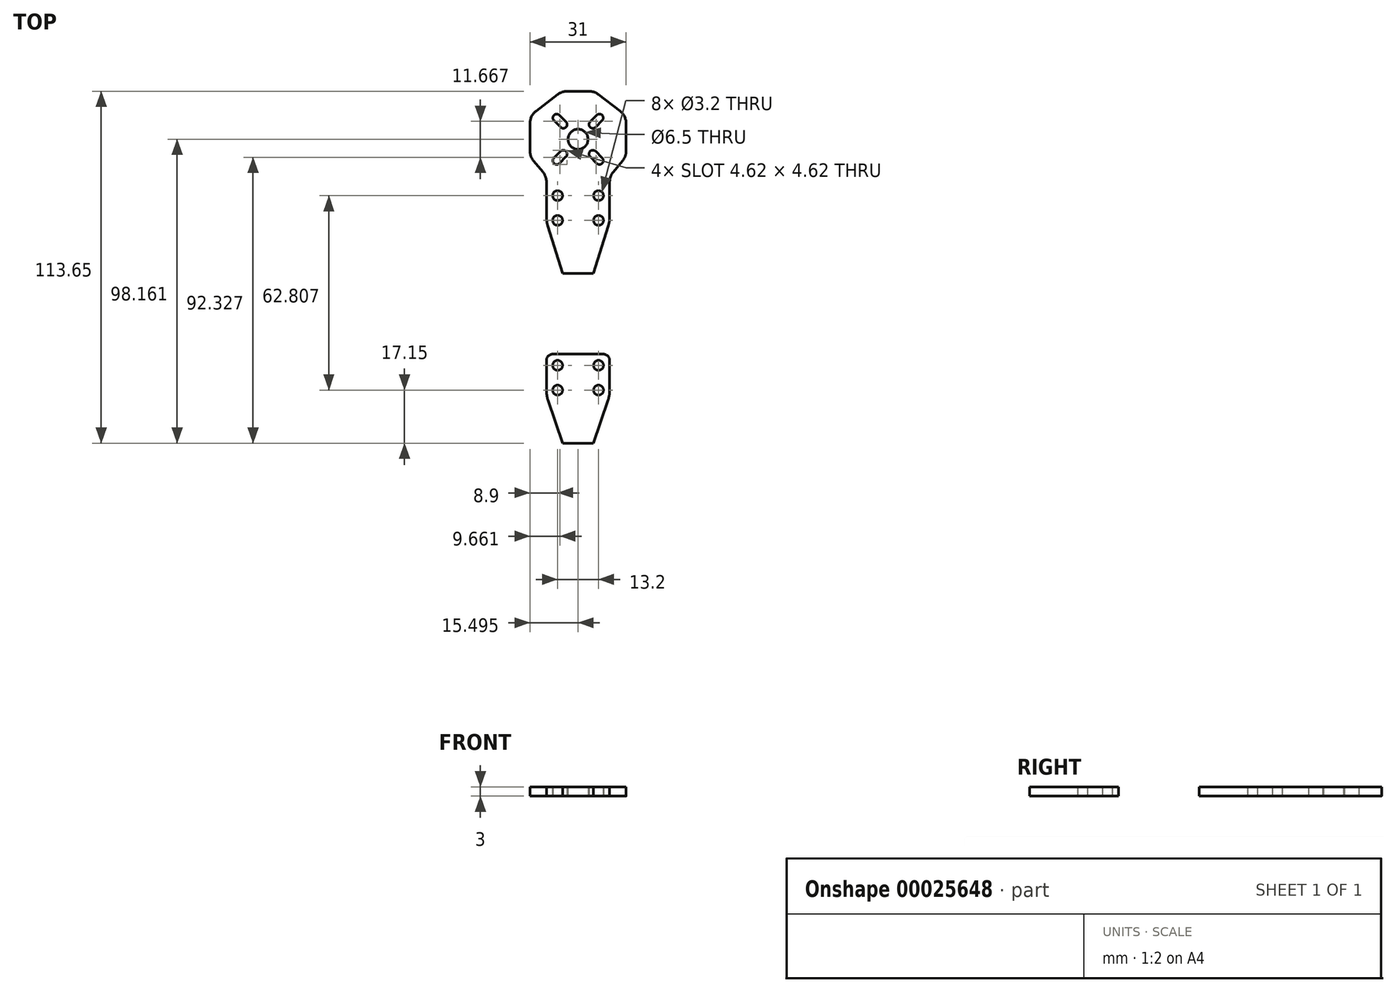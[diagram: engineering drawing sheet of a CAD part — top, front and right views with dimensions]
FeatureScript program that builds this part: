
annotation { "Feature Type Name" : "Feature", "Feature Type Description" : "" }
export const myFeature = defineFeature(function(context is Context, id is Id, definition is map)
    precondition{}
    {
        {
            var Q0;
            Q0=qCreatedBy(makeId("Top.planeOp"),FACE);
            var sketch = newSketch(context, id + "F0", { "sketchPlane" : qUnion([Q0])});
            skLineSegment(sketch, "E0", {"start": v(0, 0) * mm, "end": v(0, 77) * mm, "construction": true});
            skCircle(sketch, "E1.0", {"center": v(0, 77.01) * mm, "radius": 3.25 * mm});
            skArc(sketch, "E2.0", {"start": v(-5.66, 80.9) * mm, "mid": v(-3.9, 80.9) * mm, "end": v(-3.9, 82.67) * mm});
            skLineSegment(sketch, "E3.0", {"start": v(-3.9, 82.67) * mm, "end": v(-6.02, 84.79) * mm});
            skLineSegment(sketch, "E4.0", {"start": v(-7.78, 83.02) * mm, "end": v(-5.66, 80.9) * mm});
            skArc(sketch, "E5.0", {"start": v(-6.02, 84.79) * mm, "mid": v(-7.78, 84.79) * mm, "end": v(-7.78, 83.02) * mm});
            skLineSegment(sketch, "E6.0", {"start": v(5.65, 80.9) * mm, "end": v(7.77, 83.02) * mm});
            skLineSegment(sketch, "E7.0", {"start": v(6, 84.79) * mm, "end": v(3.88, 82.67) * mm});
            skArc(sketch, "E8.0", {"start": v(7.77, 83.02) * mm, "mid": v(7.77, 84.79) * mm, "end": v(6, 84.79) * mm});
            skArc(sketch, "E9.0", {"start": v(3.88, 82.67) * mm, "mid": v(3.88, 80.9) * mm, "end": v(5.65, 80.9) * mm});
            skLineSegment(sketch, "E10.0", {"start": v(-5.66, 73.12) * mm, "end": v(-7.78, 71) * mm});
            skArc(sketch, "E11.0", {"start": v(-3.9, 71.35) * mm, "mid": v(-3.9, 73.12) * mm, "end": v(-5.66, 73.12) * mm});
            skArc(sketch, "E12.0", {"start": v(-7.78, 71) * mm, "mid": v(-7.78, 69.23) * mm, "end": v(-6.02, 69.23) * mm});
            skLineSegment(sketch, "E13.0", {"start": v(-6.02, 69.23) * mm, "end": v(-3.9, 71.35) * mm});
            skArc(sketch, "E14.0", {"start": v(5.65, 73.12) * mm, "mid": v(3.88, 73.12) * mm, "end": v(3.88, 71.35) * mm});
            skLineSegment(sketch, "E15.0", {"start": v(7.77, 71) * mm, "end": v(5.65, 73.12) * mm});
            skLineSegment(sketch, "E16.0", {"start": v(3.88, 71.35) * mm, "end": v(6, 69.23) * mm});
            skArc(sketch, "E17.0", {"start": v(6, 69.23) * mm, "mid": v(7.77, 69.23) * mm, "end": v(7.77, 71) * mm});
            skCircle(sketch, "E18", {"center": v(0, 77) * mm, "radius": 12.5 * mm, "construction": true});
            skLineSegment(sketch, "E19.0", {"start": v(5, 0) * mm, "end": v(5, 77) * mm, "construction": true});
            skLineSegment(sketch, "E20.0", {"start": v(-5, 0) * mm, "end": v(-5, 77) * mm, "construction": true});
            skLineSegment(sketch, "E21.0", {"start": v(-6.6, 0) * mm, "end": v(-6.6, 77) * mm, "construction": true});
            skLineSegment(sketch, "E22.0", {"start": v(6.6, 0) * mm, "end": v(6.6, 77) * mm, "construction": true});
            skLineSegment(sketch, "E23", {"start": v(0, 77) * mm, "end": v(0, 92.5) * mm});
            skCircle(sketch, "E24", {"center": v(-6.6, 58.8) * mm, "radius": 1.6 * mm});
            skLineSegment(sketch, "E25", {"start": v(-15.5, 82.2) * mm, "end": v(-15.5, 73.2) * mm});
            skLineSegment(sketch, "E26", {"start": v(-14.34, 70) * mm, "end": v(-11.36, 66.42) * mm});
            skLineSegment(sketch, "E27", {"start": v(-13.53, 86.18) * mm, "end": v(-6.57, 91.48) * mm});
            skLineSegment(sketch, "E28", {"start": v(0, 92.5) * mm, "end": v(-3.54, 92.5) * mm});
            skCircle(sketch, "E29", {"center": v(-6.6, 50.8) * mm, "radius": 1.6 * mm});
            skLineSegment(sketch, "E30", {"start": v(-10.2, 51.98) * mm, "end": v(-10.2, 63.22) * mm});
            skPoint(sketch, "E31.visualSharp", {"position": v(-10.2, 65.03) * mm});
            skArc(sketch, "E31.filletArc", {"start": v(-10.2, 63.22) * mm, "mid": v(-10.5, 64.92) * mm, "end": v(-11.36, 66.42) * mm});
            skPoint(sketch, "E32.visualSharp", {"position": v(-15.5, 71.4) * mm});
            skArc(sketch, "E32.filletArc", {"start": v(-15.5, 73.2) * mm, "mid": v(-15.2, 71.5) * mm, "end": v(-14.34, 70) * mm});
            skPoint(sketch, "E33.visualSharp", {"position": v(-15.5, 84.68) * mm});
            skArc(sketch, "E33.filletArc", {"start": v(-13.53, 86.18) * mm, "mid": v(-14.98, 84.43) * mm, "end": v(-15.5, 82.2) * mm});
            skPoint(sketch, "E34.visualSharp", {"position": v(-5.23, 92.5) * mm});
            skArc(sketch, "E34.filletArc", {"start": v(-3.54, 92.5) * mm, "mid": v(-5.14, 92.24) * mm, "end": v(-6.57, 91.48) * mm});
            skLineSegment(sketch, "E35.0.MirrorCS", {"start": v(0, 92.5) * mm, "end": v(3.54, 92.5) * mm});
            skArc(sketch, "E36.0.MirrorCS", {"start": v(3.54, 92.5) * mm, "mid": v(5.14, 92.24) * mm, "end": v(6.57, 91.48) * mm});
            skLineSegment(sketch, "E37.0.MirrorCS", {"start": v(13.53, 86.18) * mm, "end": v(6.57, 91.48) * mm});
            skArc(sketch, "E38.0.MirrorCS", {"start": v(13.53, 86.18) * mm, "mid": v(14.98, 84.43) * mm, "end": v(15.5, 82.2) * mm});
            skLineSegment(sketch, "E39.0.MirrorCS", {"start": v(15.5, 82.2) * mm, "end": v(15.5, 73.2) * mm});
            skArc(sketch, "E40.0.MirrorCS", {"start": v(15.5, 73.2) * mm, "mid": v(15.2, 71.5) * mm, "end": v(14.34, 70) * mm});
            skLineSegment(sketch, "E41.0.MirrorCS", {"start": v(14.34, 70) * mm, "end": v(11.36, 66.42) * mm});
            skPoint(sketch, "E42.0.MirrorP", {"position": v(10.2, 65.03) * mm});
            skArc(sketch, "E43.0.MirrorCS", {"start": v(10.2, 63.22) * mm, "mid": v(10.5, 64.92) * mm, "end": v(11.36, 66.42) * mm});
            skLineSegment(sketch, "E44.0.MirrorCS", {"start": v(10.2, 51.98) * mm, "end": v(10.2, 63.22) * mm});
            skCircle(sketch, "E45.0.MirrorC", {"center": v(6.6, 58.8) * mm, "radius": 1.6 * mm});
            skCircle(sketch, "E46.0.MirrorC", {"center": v(6.6, 50.8) * mm, "radius": 1.6 * mm});
            skLineSegment(sketch, "E47.0", {"start": v(-6.6, 62.4) * mm, "end": v(6.6, 62.4) * mm, "construction": true});
            skLineSegment(sketch, "E48", {"start": v(-5, 33.66) * mm, "end": v(5, 33.66) * mm});
            skLineSegment(sketch, "E49.filletArc", {"start": v(-10.2, 51.22) * mm, "end": v(-10.2, 51.22) * mm});
            skLineSegment(sketch, "E50.filletArc", {"start": v(-10.2, 50.46) * mm, "end": v(-10.2, 50.46) * mm});
            skLineSegment(sketch, "E51.0.MirrorCS", {"start": v(10.2, 50.46) * mm, "end": v(10.2, 50.46) * mm});
            skLineSegment(sketch, "E52", {"start": v(-9.75, 49.02) * mm, "end": v(-5, 33.66) * mm});
            skLineSegment(sketch, "E53", {"start": v(9.75, 49.02) * mm, "end": v(5, 33.66) * mm});
            skArc(sketch, "E54.filletArc", {"start": v(-10.2, 51.98) * mm, "mid": v(-10.09, 50.48) * mm, "end": v(-9.75, 49.02) * mm});
            skArc(sketch, "E55.filletArc", {"start": v(9.75, 49.02) * mm, "mid": v(10.09, 50.48) * mm, "end": v(10.2, 51.98) * mm});
            skSolve(sketch);
        }
        {
            var Q0;
            Q0=makeQuery(id+"F0.imprint","IMPRINT",FACE,{"disambiguationData":[TD([[makeQuery(id+"F0.imprint","IMPRINT",EDGE,{"derivedFrom":sQuery(id+"F0.wireOp",EDGE,"E1.0")}),-1.0]])]});
            extrude(context, id + "F1", {"entities" : qUnion([Q0]), "depth" : 3 * mm});
        }
        {
            var Q0;
            Q0=qCreatedBy(makeId("Top.planeOp"),FACE);
            var sketch = newSketch(context, id + "F2", { "sketchPlane" : qUnion([Q0])});
            skLineSegment(sketch, "E56.rect.top", {"start": v(8.2, 7.6) * mm, "end": v(-8.2, 7.6) * mm});
            skLineSegment(sketch, "E56.rect.left", {"start": v(10.2, -4.1) * mm, "end": v(10.2, 5.6) * mm});
            skLineSegment(sketch, "E56.rect.right", {"start": v(-10.2, -4.1) * mm, "end": v(-10.2, 5.6) * mm});
            skPoint(sketch, "E56.rect.middle", {"position": v(0, 0) * mm});
            skLineSegment(sketch, "E57.0", {"start": v(-6.6, -7.6) * mm, "end": v(-6.6, 7.6) * mm, "construction": true});
            skLineSegment(sketch, "E58.0", {"start": v(10.2, 4) * mm, "end": v(-10.2, 4) * mm, "construction": true});
            skLineSegment(sketch, "E59.0", {"start": v(6.6, -7.6) * mm, "end": v(6.6, 7.6) * mm, "construction": true});
            skCircle(sketch, "E60", {"center": v(-6.6, 4) * mm, "radius": 1.6 * mm});
            skLineSegment(sketch, "E61", {"start": v(0, 0) * mm, "end": v(0, 18.36) * mm, "construction": true});
            skLineSegment(sketch, "E62", {"start": v(0, 0) * mm, "end": v(-15.12, 0) * mm, "construction": true});
            skCircle(sketch, "E63.0.MirrorC", {"center": v(6.6, 4) * mm, "radius": 1.6 * mm});
            skCircle(sketch, "E64.0.MirrorC", {"center": v(-6.6, -4) * mm, "radius": 1.6 * mm});
            skCircle(sketch, "E65.0.MirrorC", {"center": v(6.6, -4) * mm, "radius": 1.6 * mm});
            skPoint(sketch, "E66.visualSharp", {"position": v(-10.2, 7.6) * mm});
            skArc(sketch, "E66.filletArc", {"start": v(-8.2, 7.6) * mm, "mid": v(-9.61, 7.01) * mm, "end": v(-10.2, 5.6) * mm});
            skPoint(sketch, "E67.visualSharp", {"position": v(10.2, 7.6) * mm});
            skArc(sketch, "E67.filletArc", {"start": v(10.2, 5.6) * mm, "mid": v(9.61, 7.01) * mm, "end": v(8.2, 7.6) * mm});
            skLineSegment(sketch, "E68", {"start": v(-5, -21.15) * mm, "end": v(5, -21.15) * mm});
            skLineSegment(sketch, "E69", {"start": v(-9.67, -7.3) * mm, "end": v(-5, -21.15) * mm});
            skLineSegment(sketch, "E70", {"start": v(9.67, -7.3) * mm, "end": v(5, -21.15) * mm});
            skPoint(sketch, "E71.visualSharp", {"position": v(-10.2, -5.75) * mm});
            skArc(sketch, "E71.filletArc", {"start": v(-10.2, -4.1) * mm, "mid": v(-10.07, -5.72) * mm, "end": v(-9.67, -7.3) * mm});
            skPoint(sketch, "E72.visualSharp", {"position": v(10.2, -5.75) * mm});
            skArc(sketch, "E72.filletArc", {"start": v(9.67, -7.3) * mm, "mid": v(10.07, -5.72) * mm, "end": v(10.2, -4.1) * mm});
            skSolve(sketch);
        }
        {
            var Q0;
            Q0=makeQuery(id+"F2.imprint","IMPRINT",FACE,{"disambiguationData":[TD([[makeQuery(id+"F2.imprint","IMPRINT",EDGE,{"derivedFrom":sQuery(id+"F2.wireOp",EDGE,"E56.rect.top")}),1.0]])]});
            extrude(context, id + "F3", {"entities" : qUnion([Q0]), "depth" : 3 * mm});
        }
    });
